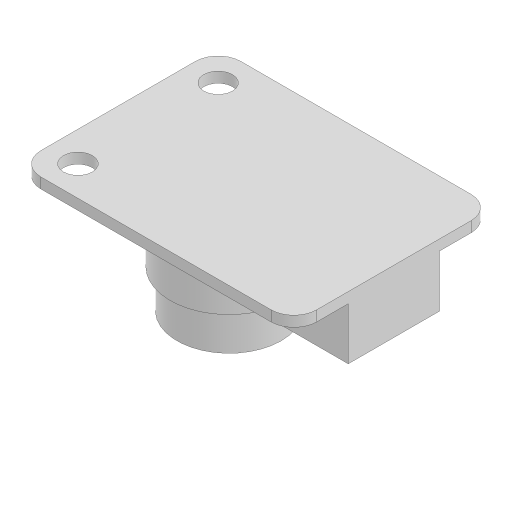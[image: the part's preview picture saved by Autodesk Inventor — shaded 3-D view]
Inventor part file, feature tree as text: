
AUTODESK INVENTOR PART (.ipt)
format: ipt  version: 2024.3 (Build 283343000, 343)  size: 532,992 bytes
history: native  units: mm
features: sketch x5, extrude x5, other x5, projected_geometry x4, fillet x1
ambient origin geometry x8: Origin, YZ Plane, XZ Plane, XY Plane, X Axis, Y Axis, Z Axis, Center Point
bodies: Solid1 (feature_tree)
feature tree (20):
  sketch  "Sketch1"  dims[d0=21.9mm d1=30.2mm]
  extrude  "Extrusion1"  Depth=30.2mm
  extrude  "Extrusion2"  Depth=18.6mm
  extrude  "Extrusion3"  Depth=8.0mm TaperAngle=0.0deg
  extrude  "Extrusion4"  Depth=4.2mm TaperAngle=0.0deg
  extrude  "Extrusion5"  Depth=8.0mm
  fillet  "Fillet1"  Radius=5.7mm
  sketch  "Sketch5"  dims[d12=10.0mm d13=8.0mm d14=5.7mm d15=0.0mm d16=3.15mm d17=3.15mm d18=4.85mm d19=3.275mm d20=3.275mm d21=4.85mm d22=0.0mm d23=0.0mm d24=2.5mm]
  other  "Decal1"
  other  "Decal2"
  other  "Decal3"
  other  "Decal4"
  sketch  "Sketch2"  dims[d3=12.9mm d4=18.6mm]
  projected_geometry  "Projected Loop1"
  sketch  "Sketch3"  dims[d5=1.15mm d6=0.0mm d7=8.0mm d8=0.0mm]
  projected_geometry  "Projected Loop2"
  sketch  "Sketch4"  dims[d9=11.4mm d10=4.2mm d11=0.0mm]
  projected_geometry  "Projected Loop3"
  projected_geometry  "Projected Loop4"
  other  "Image1"
